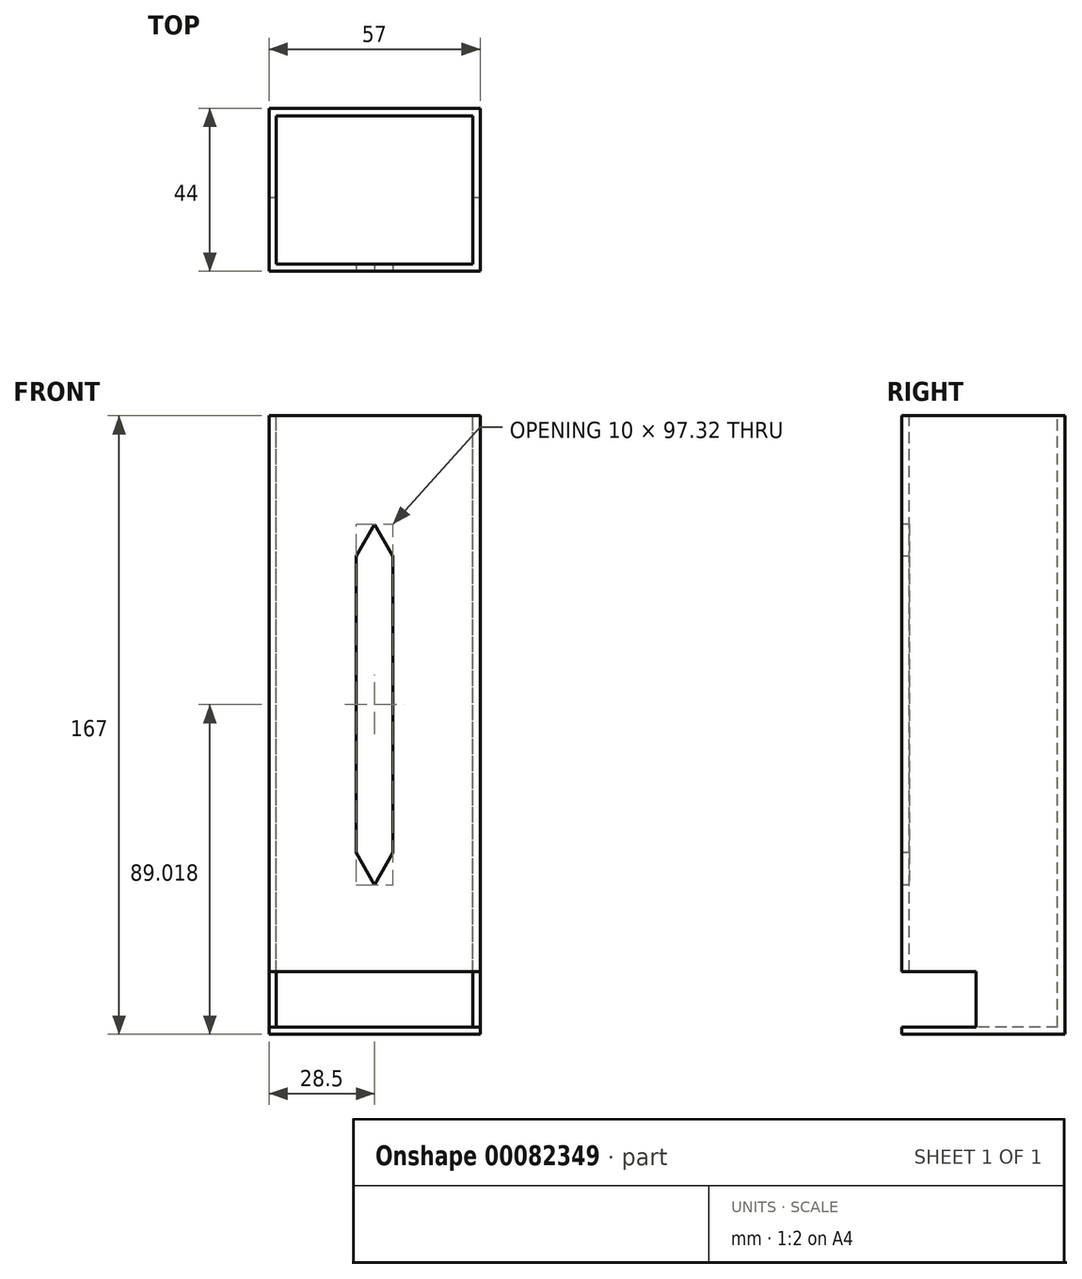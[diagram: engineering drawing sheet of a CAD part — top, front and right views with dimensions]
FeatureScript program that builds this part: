
annotation { "Feature Type Name" : "Feature", "Feature Type Description" : "" }
export const myFeature = defineFeature(function(context is Context, id is Id, definition is map)
    precondition{}
    {
        {
            var Q0;
            Q0=qCreatedBy(makeId("Top.planeOp"),FACE);
            var sketch = newSketch(context, id + "F0", { "sketchPlane" : qUnion([Q0])});
            skLineSegment(sketch, "E0.bottom", {"start": v(-28.5, 22) * mm, "end": v(28.5, 22) * mm});
            skLineSegment(sketch, "E0.top", {"start": v(-28.5, -22) * mm, "end": v(28.5, -22) * mm});
            skLineSegment(sketch, "E0.left", {"start": v(-28.5, 22) * mm, "end": v(-28.5, -22) * mm});
            skLineSegment(sketch, "E0.right", {"start": v(28.5, 22) * mm, "end": v(28.5, -22) * mm});
            skPoint(sketch, "E0.middle", {"position": v(0, 0) * mm});
            skSolve(sketch);
        }
        {
            var Q0;
            Q0=qSketchRegion(id+"F0",true);
            extrude(context, id + "F1", {"entities" : qUnion([Q0]), "depth" : 167 * mm});
        }
        {
            var Q0;
            Q0=makeQuery(id+"F1.opExtrude","CAP_FACE",FACE,{"disambiguationData":[OSD([sQuery(id+"F0.wireOp",EDGE,"E0.bottom"),sQuery(id+"F0.wireOp",EDGE,"E0.top"),sQuery(id+"F0.wireOp",EDGE,"E0.left"),sQuery(id+"F0.wireOp",EDGE,"E0.right")])],"isStart":false});
            var sketch = newSketch(context, id + "F2", { "sketchPlane" : qUnion([Q0])});
            skLineSegment(sketch, "E1.bottom", {"start": v(-26.5, 20) * mm, "end": v(26.5, 20) * mm});
            skLineSegment(sketch, "E1.top", {"start": v(-26.5, -20) * mm, "end": v(26.5, -20) * mm});
            skLineSegment(sketch, "E1.left", {"start": v(-26.5, 20) * mm, "end": v(-26.5, -20) * mm});
            skLineSegment(sketch, "E1.right", {"start": v(26.5, 20) * mm, "end": v(26.5, -20) * mm});
            skPoint(sketch, "E1.middle", {"position": v(0, 0) * mm});
            skSolve(sketch);
        }
        {
            var Q0;
            Q0=makeQuery(id+"F2.imprint","IMPRINT",FACE,{"disambiguationData":[TD([[makeQuery(id+"F2.imprint","IMPRINT",EDGE,{"derivedFrom":sQuery(id+"F2.wireOp",EDGE,"E1.bottom")}),-1.0]])]});
            extrude(context, id + "F3", {"entities" : qUnion([Q0]), "operationType" : NewBodyOperationType.REMOVE, "oppositeDirection" : true, "depth" : 165 * mm});
        }
        {
            var Q0;
            Q0=makeQuery(id+"F1.opExtrude","SWEPT_FACE",FACE,{"disambiguationData":[OSD([sQuery(id+"F0.wireOp",EDGE,"E0.right")])]});
            var sketch = newSketch(context, id + "F4", { "sketchPlane" : qUnion([Q0])});
            skLineSegment(sketch, "E2.bottom", {"start": v(-22, 17) * mm, "end": v(-2, 17) * mm});
            skLineSegment(sketch, "E2.top", {"start": v(-22, 2) * mm, "end": v(-2, 2) * mm});
            skLineSegment(sketch, "E2.left", {"start": v(-22, 17) * mm, "end": v(-22, 2) * mm});
            skLineSegment(sketch, "E2.right", {"start": v(-2, 17) * mm, "end": v(-2, 2) * mm});
            skSolve(sketch);
        }
        {
            var Q0;
            Q0=makeQuery(id+"F4.imprint","IMPRINT",FACE,{"disambiguationData":[TD([[makeQuery(id+"F4.imprint","IMPRINT",EDGE,{"derivedFrom":sQuery(id+"F4.wireOp",EDGE,"E2.bottom")}),-1.0]])]});
            extrude(context, id + "F5", {"entities" : qUnion([Q0]), "operationType" : NewBodyOperationType.REMOVE, "oppositeDirection" : true, "depth" : 84 * mm});
        }
        {
            var Q0;
            {var subQ2=sQuery(id+"F0.wireOp",EDGE,"E0.top");Q0=makeQuery(id+"F5.boolean.opBoolean","SPLIT",FACE,{"disambiguationData":[TD([makeQuery(id+"F5.opExtrude","SWEPT_FACE",FACE,{"disambiguationData":[OSD([sQuery(id+"F4.wireOp",EDGE,"E2.bottom")])]})])],"derivedFrom":makeQuery(id+"F1.opExtrude","SWEPT_FACE",FACE,{"disambiguationData":[OSD([subQ2])]})});}
            var sketch = newSketch(context, id + "F6", { "sketchPlane" : qUnion([Q0])});
            skLineSegment(sketch, "E3.bottom", {"start": v(-5, 129.02) * mm, "end": v(5, 129.02) * mm});
            skLineSegment(sketch, "E3.top", {"start": v(-5, 49.02) * mm, "end": v(5, 49.02) * mm});
            skLineSegment(sketch, "E3.left", {"start": v(-5, 129.02) * mm, "end": v(-5, 49.02) * mm});
            skLineSegment(sketch, "E3.right", {"start": v(5, 129.02) * mm, "end": v(5, 49.02) * mm});
            skPoint(sketch, "E3.middle", {"position": v(0, 89.02) * mm});
            skLineSegment(sketch, "E4", {"start": v(-5, 129.02) * mm, "end": v(0, 137.68) * mm});
            skLineSegment(sketch, "E5", {"start": v(0, 137.68) * mm, "end": v(5, 129.02) * mm});
            skLineSegment(sketch, "E6", {"start": v(-5, 49.02) * mm, "end": v(0, 40.36) * mm});
            skLineSegment(sketch, "E7", {"start": v(0, 40.36) * mm, "end": v(5, 49.02) * mm});
            skSolve(sketch);
        }
        {
            var Q0;
            Q0=makeQuery(id+"F6.imprint","IMPRINT",FACE,{"disambiguationData":[TD([[makeQuery(id+"F6.imprint","IMPRINT",EDGE,{"derivedFrom":sQuery(id+"F6.wireOp",EDGE,"E3.top")}),-1.0]])]});
            var Q1;
            Q1=makeQuery(id+"F6.imprint","IMPRINT",FACE,{"disambiguationData":[TD([[makeQuery(id+"F6.imprint","IMPRINT",EDGE,{"derivedFrom":sQuery(id+"F6.wireOp",EDGE,"E3.bottom")}),-1.0]])]});
            var Q2;
            Q2=makeQuery(id+"F6.imprint","IMPRINT",FACE,{"disambiguationData":[TD([[makeQuery(id+"F6.imprint","IMPRINT",EDGE,{"derivedFrom":sQuery(id+"F6.wireOp",EDGE,"E3.bottom")}),1.0]])]});
            extrude(context, id + "F7", {"entities" : qUnion([Q0, Q1, Q2]), "operationType" : NewBodyOperationType.REMOVE, "oppositeDirection" : true, "depth" : 2 * mm});
        }
    });
